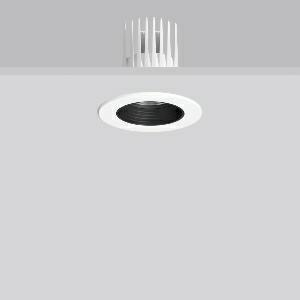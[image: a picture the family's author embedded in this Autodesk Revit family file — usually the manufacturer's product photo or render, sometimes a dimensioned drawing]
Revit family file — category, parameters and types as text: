
# Revit family: heledon_mini_e_901752_002_3_76_5bb3
name_source: partatom
category: Lighting Fixtures
units: mm (PartAtom-declared; Revit-internal decimal feet)

## family parameters
Cut with Voids When Loaded = No
Host = Face
Light Source = No
Part Type = Normal
Room Calculation Point = No
Round Connector Dimension = Use Diameter
Shared = No

## types (1)
- HELEDON mini E (1 x LED Modul 935, 3050 lm, 3500)
    Apparent Load = 29 VA
    Approval mark = CE
    CIE Flux Codes = 96 100 100 100 100
    Color Rendering = 92
    Color Temperature = 3500
    Default Elevation = 1800 mm
    Description = Series: HELEDON mini
Round recessed downlight. Housing: die-cast aluminium, powder-coated. Black plastic ring and recessed LED to prevent glare from the side. Optical assembly with lens made of plastic (polycarbonate) for the best homogeneous light distribution - can be changed without tools. Best colour rendering index Ra>90. Suitable for Recessed ceiling mounting. Installation without tools thanks to spring fastening system. Including separate LED converter with connecting cable 600 mm.High quality converter without flickering and stroboscopic effect. Through-wiring box (5 pole) available as accessory. The following accessories can be mounted without use of tools: interchangeable lenses, decorative glasses, honeycomb louvre, clear and frosted diffusers, white interchangeable plastic ring. 
Colour: traffic white, matt (RAL 9016)
Diameter: 124 mm
Height: 3 mm
Cut-out diameter: 114 mm
Recess height: 170 mm
Luminaire: recess height: 120 mm
Lamp: LED
Socket: without socket
Colour temperature: 3500K
Colour rendering index (CRI): 92
System power: 29 W
Rated luminous flux: 3050 lm
Luminous efficiency: 105 lm/W
Control gear: Converter, dimmable, DALI
Protection class: II
Type of protection: IP 20
    Height = 0 mm  [stored 0 ft]
    Lamp = 1 x LED Modul 935
    Lamp Light Flux = 3050 lm
    Lamp count = 1
    Length = 124 mm  [stored 0.406824 ft]
    Lifetime = 50000 h
    Luminous efficacy = 105 lm/W
    Manufacturer = RZB
    ModVariant = No
    Model = 901752.002.3.76
    Mounting Place = Ceiling
    Mounting Type = Recessed
    Number of Poles = 1
    OnlyDefault = Yes
    Power Factor = 1
    Product Name = HELEDON mini E
    Product group = Recessed downlights
    ProductGroupID = 402
    Protection Class = Protection class II
    Protection Degree = IP 20
    RLX_Detail_Level = 1
    RLX_Emergency_Light_Flux = 0 lm
    RLX_Emergency_Type = 0
    RLX_Emergency_Type_DB = No
    RlxData = <blob elided: 126597 chars, md5=c5c94ce4>
    Socket = socket
    Standby Power = 0 W
    System Light Flux = 3050 lm
    System Power = 29 W
    Type Comments = Product without accessories
    Type Image = 901656.002.jpg
    URL = http://relux.com
    VarID = ---
    Voltage = 230 V
    Voltage Range = 220-240 V
    Weight = 0.00 kg
    Width = 0 mm  [stored 0 ft]

note: [stored X ft] marks values corroborated as IEEE doubles in the binary element streams (Revit-internal decimal feet)

## geometry (parser evidence)
native form markers: Blend x4, Sweep x10
no freeform markers — native parametric forms only
